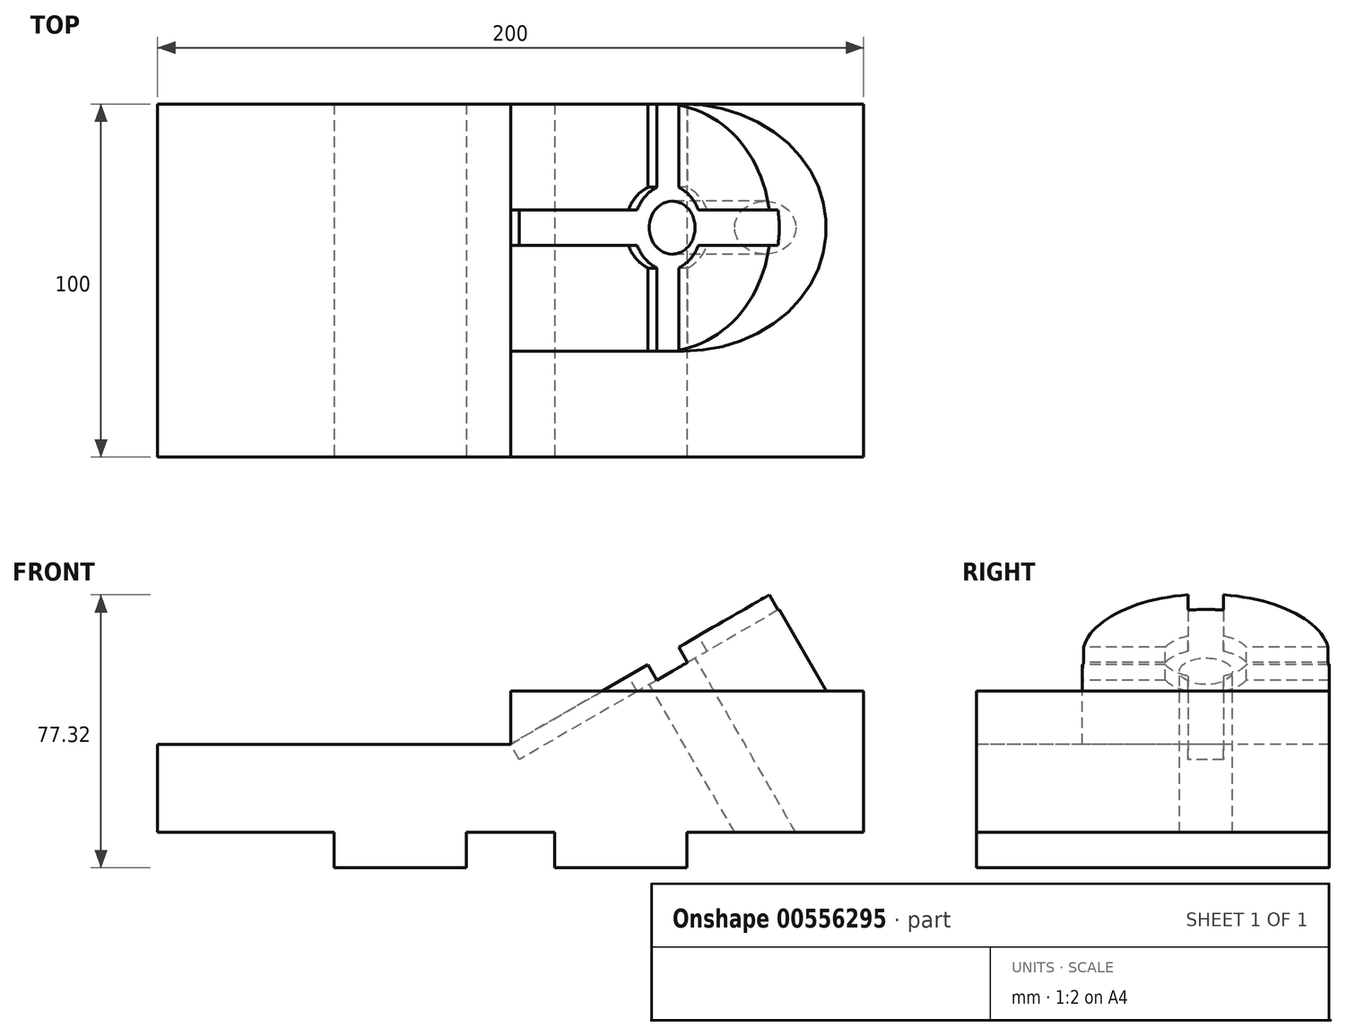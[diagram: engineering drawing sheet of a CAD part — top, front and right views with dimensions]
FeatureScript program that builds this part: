
annotation { "Feature Type Name" : "Feature", "Feature Type Description" : "" }
export const myFeature = defineFeature(function(context is Context, id is Id, definition is map)
    precondition{}
    {
        {
            var Q0;
            Q0=qCreatedBy(makeId("Front.planeOp"),FACE);
            var sketch = newSketch(context, id + "F0", { "sketchPlane" : qUnion([Q0])});
            skLineSegment(sketch, "E0", {"start": v(0, 0) * mm, "end": v(50, 0) * mm});
            skLineSegment(sketch, "E1", {"start": v(50, 0) * mm, "end": v(50, -10) * mm});
            skLineSegment(sketch, "E2", {"start": v(50, -10) * mm, "end": v(87.5, -10) * mm});
            skLineSegment(sketch, "E3", {"start": v(87.5, -10) * mm, "end": v(87.5, 0) * mm});
            skLineSegment(sketch, "E4", {"start": v(87.5, 0) * mm, "end": v(112.5, 0) * mm});
            skLineSegment(sketch, "E5", {"start": v(112.5, 0) * mm, "end": v(112.5, -10) * mm});
            skLineSegment(sketch, "E6", {"start": v(112.5, -10) * mm, "end": v(150, -10) * mm});
            skLineSegment(sketch, "E7", {"start": v(150, -10) * mm, "end": v(150, 0) * mm});
            skLineSegment(sketch, "E8", {"start": v(150, 0) * mm, "end": v(200, 0) * mm});
            skLineSegment(sketch, "E9", {"start": v(200, 0) * mm, "end": v(200, 40) * mm});
            skLineSegment(sketch, "E10", {"start": v(200, 40) * mm, "end": v(140, 40) * mm});
            skLineSegment(sketch, "E11", {"start": v(140, 40) * mm, "end": v(140, 25) * mm});
            skLineSegment(sketch, "E12", {"start": v(140, 25) * mm, "end": v(0, 25) * mm});
            skLineSegment(sketch, "E13", {"start": v(0, 25) * mm, "end": v(0, 0) * mm});
            skSolve(sketch);
        }
        {
            var Q0;
            Q0 = qSketchRegion(id + "F0", true);
            extrude(context, id + "F1", {"entities" : qUnion([Q0]), "oppositeDirection" : true, "depth" : 100 * mm, "offsetDistance" : 25 * mm});
        }
        {
            var Q0;
            Q0=makeQuery(id+"F1.opExtrude","SWEPT_FACE",FACE,{"disambiguationData":[OSD([sQuery(id+"F0.wireOp",EDGE,"E12")])]});
            var sketch = newSketch(context, id + "F2", { "sketchPlane" : qUnion([Q0])});
            skLineSegment(sketch, "E14", {"start": v(100, 100) * mm, "end": v(100, 0) * mm});
            skSolve(sketch);
        }
        {
            var Q0;
            Q0=sQuery(id+"F2.wireOp",EDGE,"E14");
            cPlane(context, id + "F3", {"entities" : qUnion([Q0]), "cplaneType" : CPlaneType.LINE_ANGLE, "offset" : 25 * mm, "angle" : 30 * degree, "width" : 150 * mm, "height" : 150 * mm});
        }
        {
            var Q0;
            Q0=qCreatedBy(id+"F3.planeOp",FACE);
            var sketch = newSketch(context, id + "F4", { "sketchPlane" : qUnion([Q0])});
            skLineSegment(sketch, "E15.bottom", {"start": v(99.1, -100) * mm, "end": v(149.1, -100) * mm});
            skLineSegment(sketch, "E15.top", {"start": v(99.1, -30) * mm, "end": v(149.1, -30) * mm});
            skLineSegment(sketch, "E15.left", {"start": v(99.1, -100) * mm, "end": v(99.1, -30) * mm});
            skArc(sketch, "E16", {"start": v(149.1, -100) * mm, "mid": v(184.1, -65) * mm, "end": v(149.1, -30) * mm});
            skSolve(sketch);
        }
        {
            var Q0;
            Q0 = qSketchRegion(id + "F4", true);
            extrude(context, id + "F5", {"entities" : qUnion([Q0]), "operationType" : NewBodyOperationType.ADD, "depth" : 40 * mm, "offsetDistance" : 25 * mm});
        }
        {
            var Q0;
            Q0=makeQuery(id+"F5.opExtrude","CAP_FACE",FACE,{"disambiguationData":[OSD([sQuery(id+"F4.wireOp",EDGE,"E15.bottom"),sQuery(id+"F4.wireOp",EDGE,"E15.top"),sQuery(id+"F4.wireOp",EDGE,"E15.left"),sQuery(id+"F4.wireOp",EDGE,"E16")])],"isStart":true});
            var sketch = newSketch(context, id + "F6", { "sketchPlane" : qUnion([Q0])});
            skLineSegment(sketch, "E17.0", {"start": v(144.1, 100) * mm, "end": v(144.1, 76.46) * mm});
            skLineSegment(sketch, "E18.0", {"start": v(154.1, 100) * mm, "end": v(154.1, 76.46) * mm});
            skLineSegment(sketch, "E19.0", {"start": v(184.1, 70) * mm, "end": v(160.56, 70) * mm});
            skLineSegment(sketch, "E20.0", {"start": v(184.1, 60) * mm, "end": v(160.56, 60) * mm});
            skLineSegment(sketch, "E21.trimOffspring", {"start": v(144.1, 53.54) * mm, "end": v(144.1, 30) * mm});
            skLineSegment(sketch, "E22.trimOffspring", {"start": v(154.1, 53.54) * mm, "end": v(154.1, 30) * mm});
            skLineSegment(sketch, "E23.trimOffspring", {"start": v(137.65, 70) * mm, "end": v(99.1, 70) * mm});
            skLineSegment(sketch, "E24.trimOffspring", {"start": v(137.65, 60) * mm, "end": v(99.1, 60) * mm});
            skArc(sketch, "E25", {"start": v(154.1, 53.54) * mm, "mid": v(157.94, 56.16) * mm, "end": v(160.56, 60) * mm});
            skArc(sketch, "E26.trimOffspring", {"start": v(160.56, 70) * mm, "mid": v(157.94, 73.84) * mm, "end": v(154.1, 76.46) * mm});
            skArc(sketch, "E27.trimOffspring", {"start": v(137.65, 60) * mm, "mid": v(140.26, 56.16) * mm, "end": v(144.1, 53.54) * mm});
            skArc(sketch, "E28.trimOffspring", {"start": v(144.1, 76.46) * mm, "mid": v(140.26, 73.84) * mm, "end": v(137.65, 70) * mm});
            skCircle(sketch, "E29", {"center": v(149.1, 65) * mm, "radius": 12.5 * mm, "construction": true});
            skLineSegment(sketch, "E30", {"start": v(99.1, 70) * mm, "end": v(99.1, 60) * mm});
            skLineSegment(sketch, "E31", {"start": v(184.1, 70) * mm, "end": v(184.1, 60) * mm});
            skLineSegment(sketch, "E32", {"start": v(154.1, 100) * mm, "end": v(144.1, 100) * mm});
            skLineSegment(sketch, "E33", {"start": v(154.1, 30) * mm, "end": v(144.1, 30) * mm});
            skSolve(sketch);
        }
        {
            var Q0;
            Q0 = qSketchRegion(id + "F6", true);
            extrude(context, id + "F7", {"entities" : qUnion([Q0]), "operationType" : NewBodyOperationType.REMOVE, "oppositeDirection" : true, "depth" : 5 * mm, "offsetDistance" : 25 * mm});
        }
        {
            var Q0;
            Q0=makeQuery(id+"F7.boolean.opBoolean","COPY",FACE,{"derivedFrom":makeQuery(id+"F7.opExtrude","CAP_FACE",FACE,{"disambiguationData":[OSD([sQuery(id+"F6.wireOp",EDGE,"E17.0"),sQuery(id+"F6.wireOp",EDGE,"E18.0"),sQuery(id+"F6.wireOp",EDGE,"E19.0"),sQuery(id+"F6.wireOp",EDGE,"E20.0"),sQuery(id+"F6.wireOp",EDGE,"E21.trimOffspring"),sQuery(id+"F6.wireOp",EDGE,"E22.trimOffspring"),sQuery(id+"F6.wireOp",EDGE,"E23.trimOffspring"),sQuery(id+"F6.wireOp",EDGE,"E24.trimOffspring"),sQuery(id+"F6.wireOp",EDGE,"E25"),sQuery(id+"F6.wireOp",EDGE,"E26.trimOffspring"),sQuery(id+"F6.wireOp",EDGE,"E27.trimOffspring"),sQuery(id+"F6.wireOp",EDGE,"E28.trimOffspring"),sQuery(id+"F6.wireOp",EDGE,"E30"),sQuery(id+"F6.wireOp",EDGE,"E31"),sQuery(id+"F6.wireOp",EDGE,"E32"),sQuery(id+"F6.wireOp",EDGE,"E33")])],"isStart":false})});
            var sketch = newSketch(context, id + "F8", { "sketchPlane" : qUnion([Q0])});
            skCircle(sketch, "E34", {"center": v(149.1, 65) * mm, "radius": 7.5 * mm});
            skSolve(sketch);
        }
        {
            var Q0;
            Q0 = qSketchRegion(id + "F8", true);
            extrude(context, id + "F9", {"entities" : qUnion([Q0]), "operationType" : NewBodyOperationType.REMOVE, "endBound" : BoundingType.THROUGH_ALL, "oppositeDirection" : true, "depth" : 25 * mm, "offsetDistance" : 25 * mm});
        }
        {
            var Q0;
            {var subQ0=sQuery(id+"F2.wireOp",EDGE,"E14");Q0=makeQuery(id+"F2.imprint","IMPRINT",FACE,{"disambiguationData":[TD([[makeQuery(id+"F2.imprint","IMPRINT",EDGE,{"derivedFrom":subQ0}),1.0]])]});}
            var sketch = newSketch(context, id + "F10", { "sketchPlane" : qUnion([Q0])});
            skLineSegment(sketch, "E35.bottom", {"start": v(100, 30) * mm, "end": v(140, 30) * mm});
            skLineSegment(sketch, "E35.top", {"start": v(100, 0) * mm, "end": v(140, 0) * mm});
            skLineSegment(sketch, "E35.left", {"start": v(100, 30) * mm, "end": v(100, 0) * mm});
            skLineSegment(sketch, "E35.right", {"start": v(140, 30) * mm, "end": v(140, 0) * mm});
            skSolve(sketch);
        }
        {
            var Q0;
            Q0 = qSketchRegion(id + "F10", true);
            var Q1;
            Q1=makeQuery(id+"F1.opExtrude","SWEPT_FACE",FACE,{"disambiguationData":[OSD([sQuery(id+"F0.wireOp",EDGE,"E10")])]});
            extrude(context, id + "F11", {"entities" : qUnion([Q0]), "operationType" : NewBodyOperationType.ADD, "endBound" : BoundingType.UP_TO_SURFACE, "depth" : 25 * mm, "endBoundEntityFace" : qUnion([Q1]), "offsetDistance" : 25 * mm});
        }
    });
